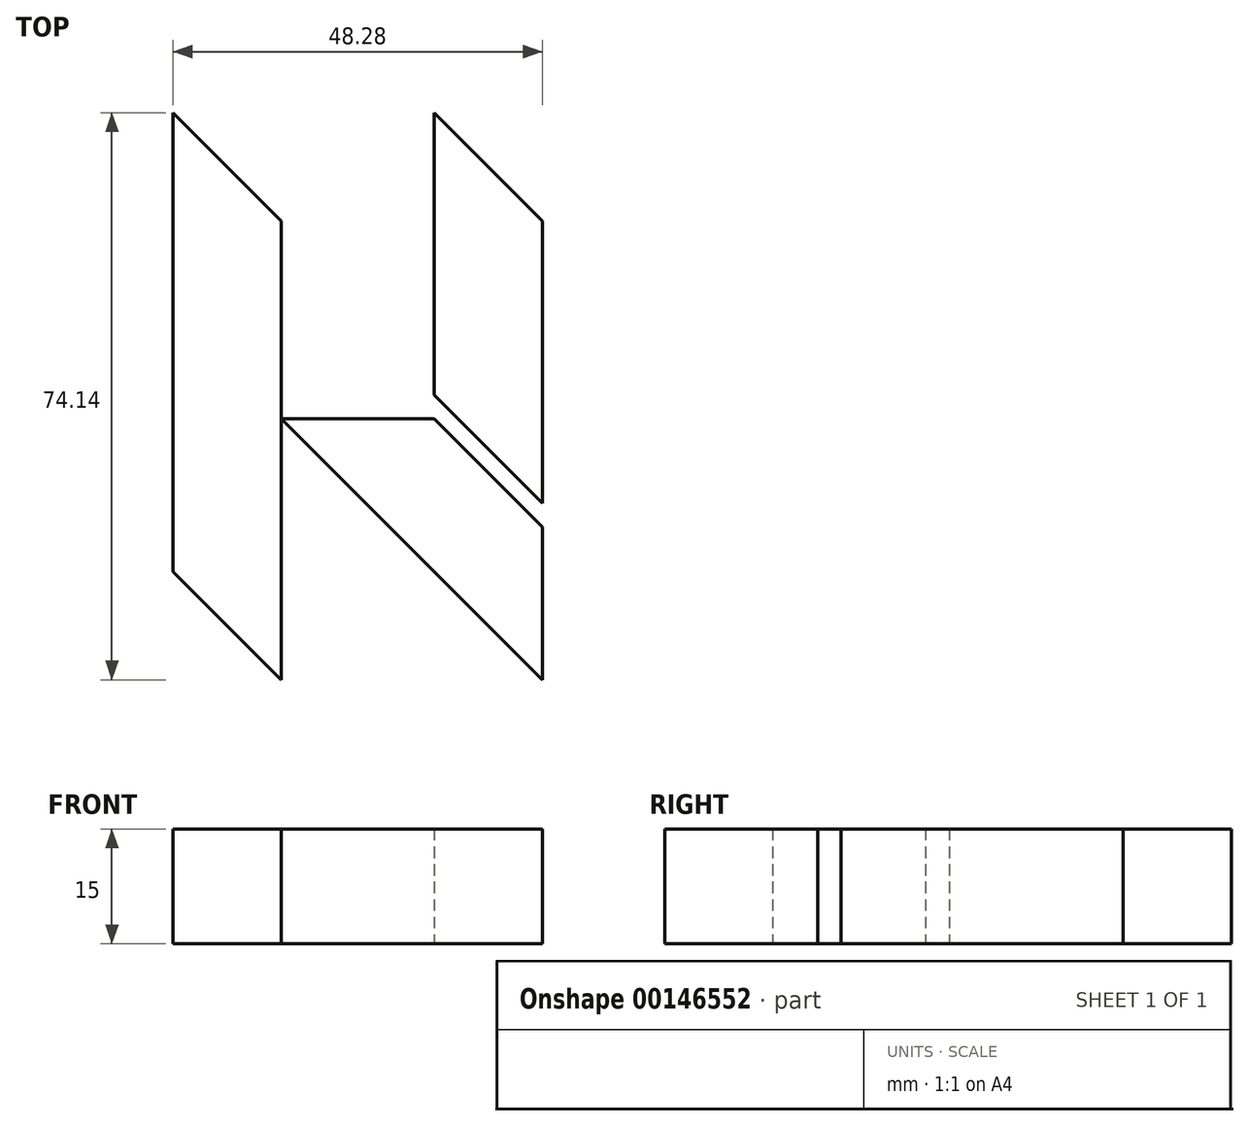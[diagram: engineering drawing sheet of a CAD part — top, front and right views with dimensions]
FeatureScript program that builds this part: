
annotation { "Feature Type Name" : "Feature", "Feature Type Description" : "" }
export const myFeature = defineFeature(function(context is Context, id is Id, definition is map)
    precondition{}
    {
        {
            var Q0;
            Q0=qCreatedBy(makeId("Top.planeOp"),FACE);
            var sketch = newSketch(context, id + "F0", { "sketchPlane" : qUnion([Q0])});
            skLineSegment(sketch, "E0.right", {"start": v(-34.14, 40) * mm, "end": v(-34.14, -20) * mm});
            skLineSegment(sketch, "E1", {"start": v(-34.14, 40) * mm, "end": v(-20, 25.86) * mm});
            skLineSegment(sketch, "E2", {"start": v(-34.14, -20) * mm, "end": v(-20, -34.14) * mm});
            skLineSegment(sketch, "E3", {"start": v(-20, 25.86) * mm, "end": v(-20, -34.14) * mm});
            skLineSegment(sketch, "E4", {"start": v(-34.14, -20) * mm, "end": v(63.5, -20) * mm, "construction": true});
            skLineSegment(sketch, "E5", {"start": v(-34.14, 40) * mm, "end": v(62.6, 40) * mm, "construction": true});
            skLineSegment(sketch, "E6", {"start": v(-20, -34.14) * mm, "end": v(59.9, -34.14) * mm, "construction": true});
            skLineSegment(sketch, "E7", {"start": v(-20, 25.86) * mm, "end": v(60.56, 25.86) * mm, "construction": true});
            skLineSegment(sketch, "E8", {"start": v(14.14, -34.14) * mm, "end": v(-20, 0) * mm});
            skLineSegment(sketch, "E9", {"start": v(-20, 0) * mm, "end": v(0, 0) * mm});
            skLineSegment(sketch, "E10", {"start": v(0, 0) * mm, "end": v(14.14, -14.14) * mm});
            skLineSegment(sketch, "E11", {"start": v(14.14, -34.14) * mm, "end": v(14.14, -14.14) * mm});
            skLineSegment(sketch, "E12", {"start": v(0, 40) * mm, "end": v(0, 3.08) * mm});
            skLineSegment(sketch, "E13", {"start": v(0, 3.08) * mm, "end": v(14.14, -11.06) * mm});
            skLineSegment(sketch, "E14", {"start": v(14.14, -11.06) * mm, "end": v(14.14, 25.86) * mm});
            skLineSegment(sketch, "E15", {"start": v(14.14, 25.86) * mm, "end": v(0, 40) * mm});
            skSolve(sketch);
        }
        {
            var Q0;
            Q0=makeQuery(id+"F0.imprint","IMPRINT",FACE,{"disambiguationData":[TD([[makeQuery(id+"F0.imprint","IMPRINT",EDGE,{"derivedFrom":sQuery(id+"F0.wireOp",EDGE,"E0.right")}),1.0]])]});
            var Q1;
            Q1=makeQuery(id+"F0.imprint","IMPRINT",FACE,{"disambiguationData":[TD([[makeQuery(id+"F0.imprint","IMPRINT",EDGE,{"derivedFrom":sQuery(id+"F0.wireOp",EDGE,"E12")}),1.0]])]});
            var Q2;
            Q2=makeQuery(id+"F0.imprint","IMPRINT",FACE,{"disambiguationData":[TD([[makeQuery(id+"F0.imprint","IMPRINT",EDGE,{"derivedFrom":sQuery(id+"F0.wireOp",EDGE,"E8")}),-1.0]])]});
            extrude(context, id + "F1", {"entities" : qUnion([Q0, Q1, Q2]), "depth" : 15 * mm});
        }
    });
